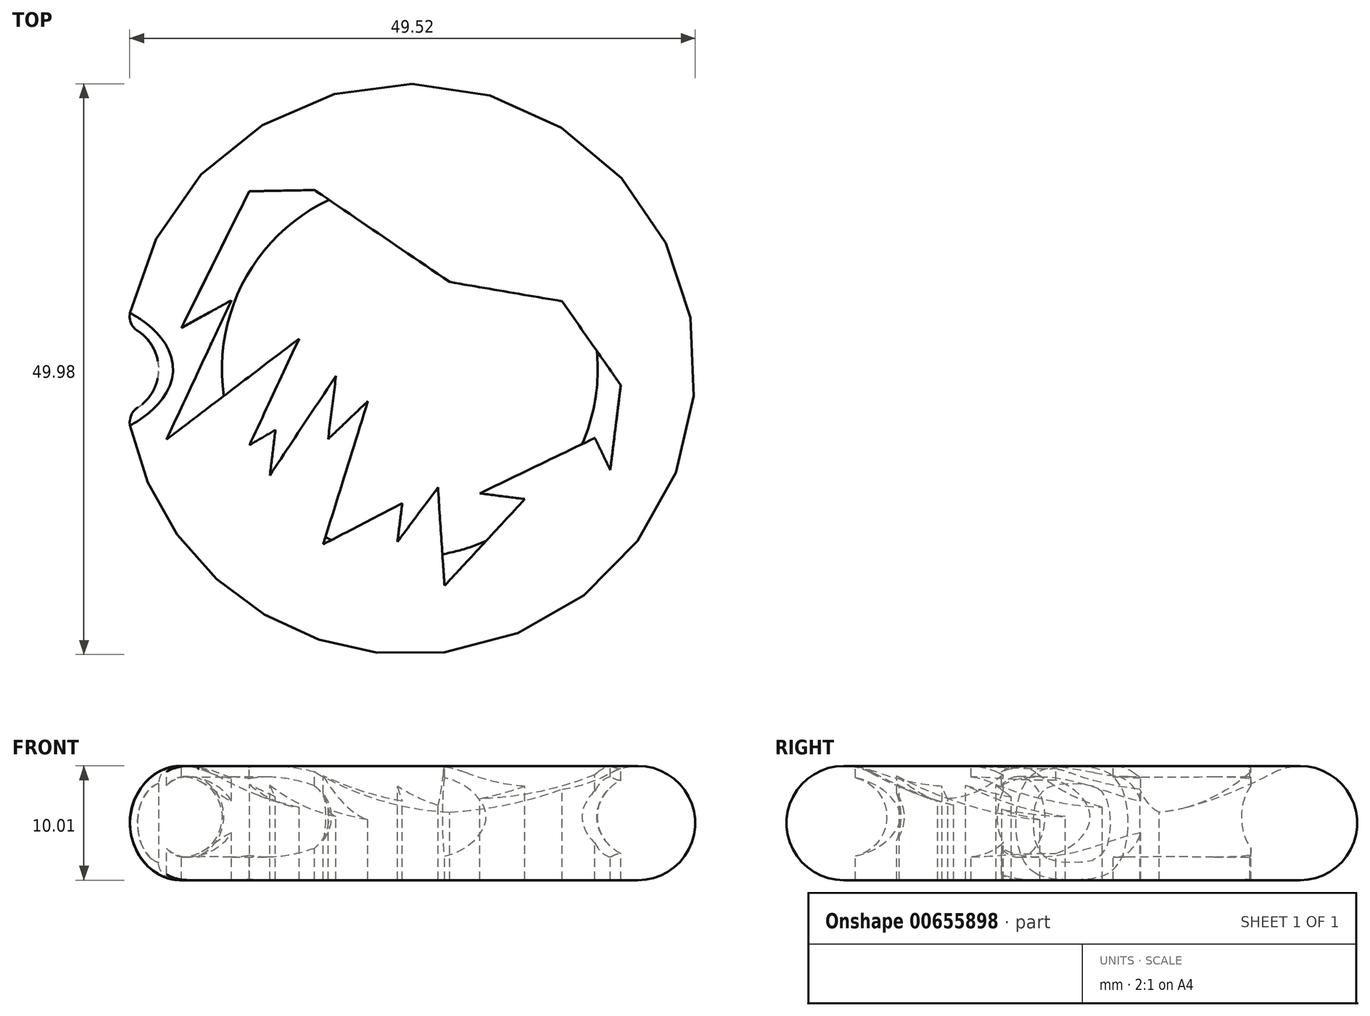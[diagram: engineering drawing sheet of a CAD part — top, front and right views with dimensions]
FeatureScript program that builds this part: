
annotation { "Feature Type Name" : "Feature", "Feature Type Description" : "" }
export const myFeature = defineFeature(function(context is Context, id is Id, definition is map)
    precondition{}
    {
        {
            var Q0;
            Q0=qCreatedBy(makeId("Front.planeOp"),FACE);
            var sketch = newSketch(context, id + "F0", { "sketchPlane" : qUnion([Q0])});
            skArc(sketch, "E0", {"start": v(-17.63, 9.41) * mm, "mid": v(-9.09, 6.12) * mm, "end": v(0, 5) * mm});
            skArc(sketch, "E1", {"start": v(-17.63, 9.41) * mm, "mid": v(-24.84, 6.21) * mm, "end": v(-19.99, 0) * mm});
            skLineSegment(sketch, "E2", {"start": v(-20, 0) * mm, "end": v(0, 0) * mm});
            skLineSegment(sketch, "E3", {"start": v(0, 0) * mm, "end": v(0, 5) * mm});
            skSolve(sketch);
        }
        {
            var Q0;
            Q0=makeQuery(id+"F0.imprint","IMPRINT",FACE,{"disambiguationData":[TD([[makeQuery(id+"F0.imprint","IMPRINT",EDGE,{"derivedFrom":sQuery(id+"F0.wireOp",EDGE,"E0")}),-1.0]])]});
            var Q1;
            Q1=sQuery(id+"F0.wireOp",EDGE,"E3");
            revolve(context, id + "F1", {"entities" : qUnion([Q0]), "axis" : qUnion([Q1]), "revolveType" : RevolveType.FULL});
        }
        {
            var Q0;
            Q0=qCreatedBy(makeId("Top.planeOp"),FACE);
            cPlane(context, id + "F2", {"entities" : qUnion([Q0]), "cplaneType" : CPlaneType.OFFSET, "offset" : 10 * mm, "width" : 150 * mm, "height" : 150 * mm});
        }
        {
            var Q0;
            Q0=qCreatedBy(id+"F2.planeOp",FACE);
            var sketch = newSketch(context, id + "F3", { "sketchPlane" : qUnion([Q0])});
            skLineSegment(sketch, "E4", {"start": v(-21.3, -6.16) * mm, "end": v(-15.61, 6.04) * mm});
            skLineSegment(sketch, "E5", {"start": v(-15.61, 6.04) * mm, "end": v(-20, 3.62) * mm});
            skLineSegment(sketch, "E6", {"start": v(-20, 3.62) * mm, "end": v(-14.06, 15.59) * mm});
            skLineSegment(sketch, "E7", {"start": v(-14.06, 15.59) * mm, "end": v(-8.34, 15.7) * mm});
            skLineSegment(sketch, "E8", {"start": v(-8.34, 15.7) * mm, "end": v(3.5, 7.64) * mm});
            skLineSegment(sketch, "E9", {"start": v(3.5, 7.64) * mm, "end": v(13.33, 5.95) * mm});
            skLineSegment(sketch, "E10", {"start": v(13.33, 5.95) * mm, "end": v(18.48, -1.4) * mm});
            skLineSegment(sketch, "E11", {"start": v(18.48, -1.4) * mm, "end": v(17.55, -8.82) * mm});
            skLineSegment(sketch, "E12", {"start": v(17.55, -8.82) * mm, "end": v(16.2, -6.02) * mm});
            skLineSegment(sketch, "E13", {"start": v(16.2, -6.02) * mm, "end": v(6.11, -10.87) * mm});
            skLineSegment(sketch, "E14", {"start": v(6.11, -10.87) * mm, "end": v(10.08, -11.37) * mm});
            skLineSegment(sketch, "E15", {"start": v(10.08, -11.37) * mm, "end": v(3.04, -18.96) * mm});
            skLineSegment(sketch, "E16", {"start": v(3.04, -18.96) * mm, "end": v(2.46, -10.36) * mm});
            skLineSegment(sketch, "E17", {"start": v(2.46, -10.36) * mm, "end": v(-1.08, -15.1) * mm});
            skLineSegment(sketch, "E18", {"start": v(-1.08, -15.1) * mm, "end": v(-0.66, -11.75) * mm});
            skLineSegment(sketch, "E19", {"start": v(-0.66, -11.75) * mm, "end": v(-7.59, -15.33) * mm});
            skLineSegment(sketch, "E20", {"start": v(-7.59, -15.33) * mm, "end": v(-3.67, -2.79) * mm});
            skLineSegment(sketch, "E21", {"start": v(-3.67, -2.79) * mm, "end": v(-7.15, -6.12) * mm});
            skLineSegment(sketch, "E22", {"start": v(-7.15, -6.12) * mm, "end": v(-6.46, -0.58) * mm});
            skLineSegment(sketch, "E23", {"start": v(-6.46, -0.58) * mm, "end": v(-12.26, -9.3) * mm});
            skLineSegment(sketch, "E24", {"start": v(-12.26, -9.3) * mm, "end": v(-11.76, -5.3) * mm});
            skLineSegment(sketch, "E25", {"start": v(-11.76, -5.3) * mm, "end": v(-14.04, -6.65) * mm});
            skLineSegment(sketch, "E26", {"start": v(-14.04, -6.65) * mm, "end": v(-9.7, 2.68) * mm});
            skLineSegment(sketch, "E27", {"start": v(-9.7, 2.68) * mm, "end": v(-21.3, -6.16) * mm});
            skLineSegment(sketch, "E28.0", {"start": v(-20, 3.62) * mm, "end": v(13.53, -12.02) * mm, "construction": true});
            skLineSegment(sketch, "E28.1", {"start": v(13.53, -12.02) * mm, "end": v(18.48, -1.4) * mm, "construction": true});
            skSolve(sketch);
        }
        {
            var Q0;
            Q0 = qSketchRegion(id + "F3", true);
            extrude(context, id + "F4", {"entities" : qUnion([Q0]), "operationType" : NewBodyOperationType.REMOVE, "oppositeDirection" : true, "depth" : 25 * mm, "offsetDistance" : 25 * mm});
        }
        {
            var Q0;
            Q0=qCreatedBy(makeId("Front.planeOp"),FACE);
            var sketch = newSketch(context, id + "F5", { "sketchPlane" : qUnion([Q0])});
            skCircle(sketch, "E29", {"center": v(-19.98, 5.54) * mm, "radius": 3.52 * mm});
            skSolve(sketch);
        }
        {
            var Q0;
            Q0 = qSketchRegion(id + "F5", true);
            var Q1;
            Q1=sQuery(id+"F0.wireOp",EDGE,"E3");
            revolve(context, id + "F6", {"operationType" : NewBodyOperationType.ADD, "entities" : qUnion([Q0]), "axis" : qUnion([Q1]), "revolveType" : RevolveType.FULL});
        }
        {
            var Q0;
            Q0=qCreatedBy(makeId("Top.planeOp"),FACE);
            var sketch = newSketch(context, id + "F7", { "sketchPlane" : qUnion([Q0])});
            skCircle(sketch, "E30", {"center": v(-26, 0) * mm, "radius": 4 * mm});
            skSolve(sketch);
        }
        {
            var Q0;
            Q0=makeQuery(id+"F7.imprint","IMPRINT",FACE,{"disambiguationData":[TD([[makeQuery(id+"F7.imprint","IMPRINT",EDGE,{"derivedFrom":sQuery(id+"F7.wireOp",EDGE,"E30")}),1.0]])]});
            extrude(context, id + "F8", {"entities" : qUnion([Q0]), "operationType" : NewBodyOperationType.REMOVE, "depth" : 25 * mm, "offsetDistance" : 25 * mm});
        }
        {
            var Q0;
            Q0=makeQuery(id+"F8.boolean.opBoolean","INTERSECT",EDGE,{"derivedFrom":[makeQuery(id+"F1.opRevolve","SWEPT_FACE",FACE,{"disambiguationData":[OSD([sQuery(id+"F0.wireOp",EDGE,"E1")])]}),makeQuery(id+"F8.opExtrude","SWEPT_FACE",FACE,{"disambiguationData":[OSD([sQuery(id+"F7.wireOp",EDGE,"E30")])]})]});
            fillet(context, id + "F9", {"entities" : qUnion([Q0]), "radius" : 1.5 * mm, "tangentPropagation" : true, "allowEdgeOverflow" : false});
        }
    });
